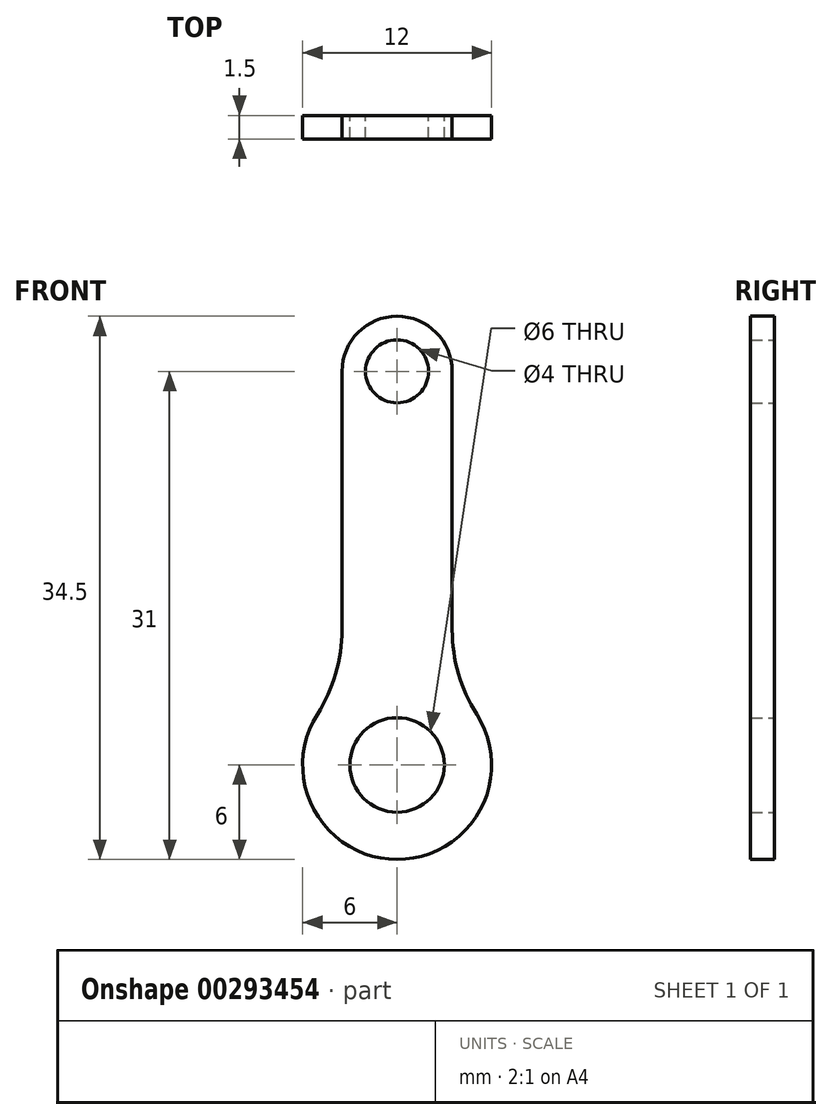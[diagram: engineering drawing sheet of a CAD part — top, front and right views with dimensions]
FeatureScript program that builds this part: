
annotation { "Feature Type Name" : "Feature", "Feature Type Description" : "" }
export const myFeature = defineFeature(function(context is Context, id is Id, definition is map)
    precondition{}
    {
        {
            var Q0;
            Q0=qCreatedBy(makeId("Front.planeOp"),FACE);
            var sketch = newSketch(context, id + "F0", { "sketchPlane" : qUnion([Q0])});
            skCircle(sketch, "E0", {"center": v(0, 0) * mm, "radius": 3 * mm});
            skCircle(sketch, "E1", {"center": v(0, 25) * mm, "radius": 2 * mm});
            skLineSegment(sketch, "E2", {"start": v(-3.5, 25) * mm, "end": v(-3.5, 8.59) * mm});
            skLineSegment(sketch, "E3", {"start": v(3.5, 25) * mm, "end": v(3.5, 8.59) * mm});
            skPoint(sketch, "E4.visualSharp", {"position": v(-3.5, 4.87) * mm});
            skPoint(sketch, "E5.visualSharp", {"position": v(3.5, 4.87) * mm});
            skArc(sketch, "E6", {"start": v(3.5, 25) * mm, "mid": v(0, 28.5) * mm, "end": v(-3.5, 25) * mm});
            skLineSegment(sketch, "E7", {"start": v(0, -11.8) * mm, "end": v(0, 8.32) * mm, "construction": true});
            skArc(sketch, "E8", {"start": v(-5.06, 3.22) * mm, "mid": v(0, -6) * mm, "end": v(5.06, 3.22) * mm});
            skArc(sketch, "E9.filletArc", {"start": v(-5.06, 3.22) * mm, "mid": v(-3.9, 5.8) * mm, "end": v(-3.5, 8.59) * mm});
            skArc(sketch, "E10.filletArc", {"start": v(3.5, 8.59) * mm, "mid": v(3.9, 5.8) * mm, "end": v(5.06, 3.22) * mm});
            skSolve(sketch);
        }
        {
            var Q0;
            Q0=makeQuery(id+"F0.imprint","IMPRINT",FACE,{"disambiguationData":[TD([[makeQuery(id+"F0.imprint","IMPRINT",EDGE,{"derivedFrom":sQuery(id+"F0.wireOp",EDGE,"E0")}),-1.0]])]});
            extrude(context, id + "F1", {"entities" : qUnion([Q0]), "depth" : 1.5 * mm});
        }
    });
